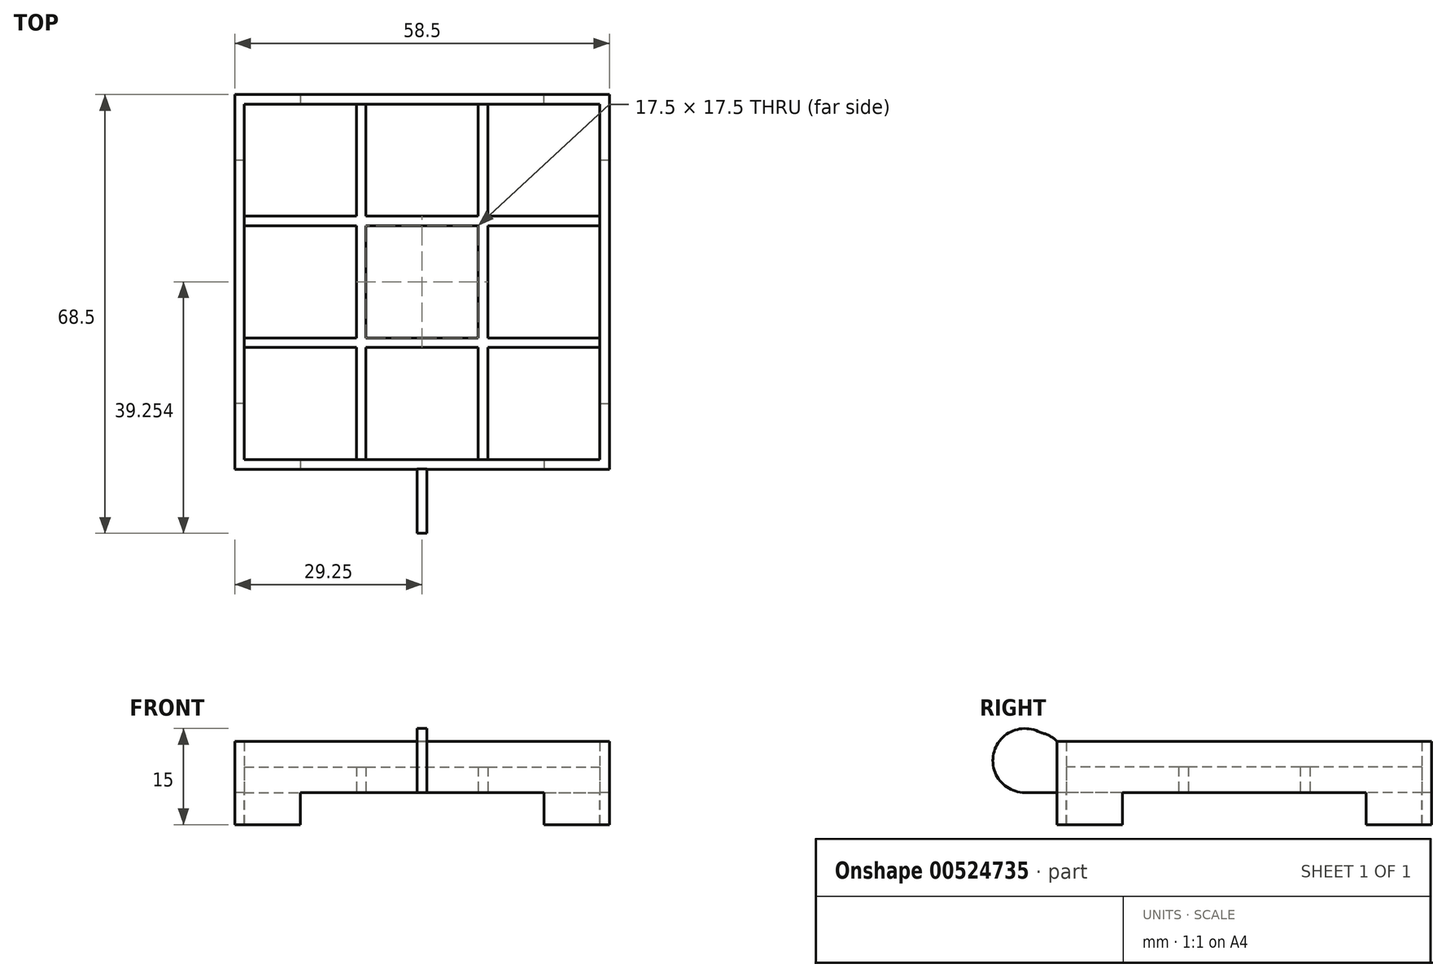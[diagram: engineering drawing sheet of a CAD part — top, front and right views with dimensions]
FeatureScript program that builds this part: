
annotation { "Feature Type Name" : "Feature", "Feature Type Description" : "" }
export const myFeature = defineFeature(function(context is Context, id is Id, definition is map)
    precondition{}
    {
        {
            var Q0;
            Q0=qCreatedBy(makeId("Top.planeOp"),FACE);
            var sketch = newSketch(context, id + "F0", { "sketchPlane" : qUnion([Q0])});
            skLineSegment(sketch, "E0.bottom", {"start": v(-41.53, 34.87) * mm, "end": v(-24.03, 34.87) * mm});
            skLineSegment(sketch, "E0.top", {"start": v(-41.53, 17.37) * mm, "end": v(-24.03, 17.37) * mm});
            skLineSegment(sketch, "E0.left", {"start": v(-41.53, 34.87) * mm, "end": v(-41.53, 17.37) * mm});
            skLineSegment(sketch, "E0.right", {"start": v(-24.03, 34.87) * mm, "end": v(-24.03, 17.37) * mm});
            skLineSegment(sketch, "E1.0.1.0", {"start": v(-41.53, 15.87) * mm, "end": v(-41.53, -1.63) * mm});
            skLineSegment(sketch, "E1.0.1.1", {"start": v(-41.53, -1.63) * mm, "end": v(-24.03, -1.63) * mm});
            skLineSegment(sketch, "E1.0.1.2", {"start": v(-24.03, 15.87) * mm, "end": v(-24.03, -1.63) * mm});
            skLineSegment(sketch, "E1.0.1.3", {"start": v(-41.53, 15.87) * mm, "end": v(-24.03, 15.87) * mm});
            skLineSegment(sketch, "E1.0.2.0", {"start": v(-41.53, -3.13) * mm, "end": v(-41.53, -20.63) * mm});
            skLineSegment(sketch, "E1.0.2.1", {"start": v(-41.53, -20.63) * mm, "end": v(-24.03, -20.63) * mm});
            skLineSegment(sketch, "E1.0.2.2", {"start": v(-24.03, -3.13) * mm, "end": v(-24.03, -20.63) * mm});
            skLineSegment(sketch, "E1.0.2.3", {"start": v(-41.53, -3.13) * mm, "end": v(-24.03, -3.13) * mm});
            skLineSegment(sketch, "E1.1.0.0", {"start": v(-22.53, 34.87) * mm, "end": v(-22.53, 17.37) * mm});
            skLineSegment(sketch, "E1.1.0.1", {"start": v(-22.53, 17.37) * mm, "end": v(-5.03, 17.37) * mm});
            skLineSegment(sketch, "E1.1.0.2", {"start": v(-5.03, 34.87) * mm, "end": v(-5.03, 17.37) * mm});
            skLineSegment(sketch, "E1.1.0.3", {"start": v(-22.53, 34.87) * mm, "end": v(-5.03, 34.87) * mm});
            skLineSegment(sketch, "E1.1.1.0", {"start": v(-22.53, 15.87) * mm, "end": v(-22.53, -1.63) * mm});
            skLineSegment(sketch, "E1.1.1.1", {"start": v(-22.53, -1.63) * mm, "end": v(-5.03, -1.63) * mm});
            skLineSegment(sketch, "E1.1.1.2", {"start": v(-5.03, 15.87) * mm, "end": v(-5.03, -1.63) * mm});
            skLineSegment(sketch, "E1.1.1.3", {"start": v(-22.53, 15.87) * mm, "end": v(-5.03, 15.87) * mm});
            skLineSegment(sketch, "E1.1.2.0", {"start": v(-22.53, -3.13) * mm, "end": v(-22.53, -20.63) * mm});
            skLineSegment(sketch, "E1.1.2.1", {"start": v(-22.53, -20.63) * mm, "end": v(-5.03, -20.63) * mm});
            skLineSegment(sketch, "E1.1.2.2", {"start": v(-5.03, -3.13) * mm, "end": v(-5.03, -20.63) * mm});
            skLineSegment(sketch, "E1.1.2.3", {"start": v(-22.53, -3.13) * mm, "end": v(-5.03, -3.13) * mm});
            skLineSegment(sketch, "E1.2.0.0", {"start": v(-3.53, 34.87) * mm, "end": v(-3.53, 17.37) * mm});
            skLineSegment(sketch, "E1.2.0.1", {"start": v(-3.53, 17.37) * mm, "end": v(13.97, 17.37) * mm});
            skLineSegment(sketch, "E1.2.0.2", {"start": v(13.97, 34.87) * mm, "end": v(13.97, 17.37) * mm});
            skLineSegment(sketch, "E1.2.0.3", {"start": v(-3.53, 34.87) * mm, "end": v(13.97, 34.87) * mm});
            skLineSegment(sketch, "E1.2.1.0", {"start": v(-3.53, 15.87) * mm, "end": v(-3.53, -1.63) * mm});
            skLineSegment(sketch, "E1.2.1.1", {"start": v(-3.53, -1.63) * mm, "end": v(13.97, -1.63) * mm});
            skLineSegment(sketch, "E1.2.1.2", {"start": v(13.97, 15.87) * mm, "end": v(13.97, -1.63) * mm});
            skLineSegment(sketch, "E1.2.1.3", {"start": v(-3.53, 15.87) * mm, "end": v(13.97, 15.87) * mm});
            skLineSegment(sketch, "E1.2.2.0", {"start": v(-3.53, -3.13) * mm, "end": v(-3.53, -20.63) * mm});
            skLineSegment(sketch, "E1.2.2.1", {"start": v(-3.53, -20.63) * mm, "end": v(13.97, -20.63) * mm});
            skLineSegment(sketch, "E1.2.2.2", {"start": v(13.97, -3.13) * mm, "end": v(13.97, -20.63) * mm});
            skLineSegment(sketch, "E1.2.2.3", {"start": v(-3.53, -3.13) * mm, "end": v(13.97, -3.13) * mm});
            skLineSegment(sketch, "E1.direction1", {"start": v(-41.53, 17.37) * mm, "end": v(-22.53, 17.37) * mm, "construction": true});
            skLineSegment(sketch, "E1.direction2", {"start": v(-41.53, 17.37) * mm, "end": v(-41.53, -1.63) * mm, "construction": true});
            skLineSegment(sketch, "E2.bottom", {"start": v(-43.03, 36.37) * mm, "end": v(15.47, 36.37) * mm});
            skLineSegment(sketch, "E2.top", {"start": v(-43.03, -22.13) * mm, "end": v(15.47, -22.13) * mm});
            skLineSegment(sketch, "E2.left", {"start": v(-43.03, 36.37) * mm, "end": v(-43.03, -22.13) * mm});
            skLineSegment(sketch, "E2.right", {"start": v(15.47, 36.37) * mm, "end": v(15.47, -22.13) * mm});
            skSolve(sketch);
        }
        {
            var Q0;
            Q0=makeQuery(id+"F0.imprint","IMPRINT",FACE,{"disambiguationData":[TD([[makeQuery(id+"F0.imprint","IMPRINT",EDGE,{"derivedFrom":sQuery(id+"F0.wireOp",EDGE,"E0.bottom")}),1.0]])]});
            extrude(context, id + "F1", {"entities" : qUnion([Q0]), "depth" : 4 * mm, "offsetDistance" : 25 * mm});
        }
        {
            var Q0;
            Q0=makeQuery(id+"F1.opExtrude","SWEPT_FACE",FACE,{"disambiguationData":[OSD([sQuery(id+"F0.wireOp",EDGE,"E2.top")])]});
            var sketch = newSketch(context, id + "F2", { "sketchPlane" : qUnion([Q0])});
            skLineSegment(sketch, "E3.bottom", {"start": v(-14.53, 0) * mm, "end": v(-13.03, 0) * mm});
            skLineSegment(sketch, "E3.top", {"start": v(-14.53, 10) * mm, "end": v(-13.03, 10) * mm});
            skLineSegment(sketch, "E3.left", {"start": v(-14.53, 0) * mm, "end": v(-14.53, 10) * mm});
            skLineSegment(sketch, "E3.right", {"start": v(-13.03, 0) * mm, "end": v(-13.03, 10) * mm});
            skSolve(sketch);
        }
        {
            var Q0;
            Q0 = qSketchRegion(id + "F2", true);
            extrude(context, id + "F3", {"entities" : qUnion([Q0]), "operationType" : NewBodyOperationType.ADD, "depth" : 10 * mm, "offsetDistance" : 25 * mm});
        }
        {
            var Q0;
            Q0=makeQuery(id+"F3.opExtrude","CAP_EDGE",EDGE,{"disambiguationData":[OSD([sQuery(id+"F2.wireOp",EDGE,"E3.top")])],"isStart":false});
            var Q1;
            Q1=makeQuery(id+"F3.opExtrude","CAP_EDGE",EDGE,{"disambiguationData":[OSD([sQuery(id+"F2.wireOp",EDGE,"E3.bottom")])],"isStart":false});
            var Q2;
            Q2=makeQuery(id+"F3.opExtrude","CAP_EDGE",EDGE,{"disambiguationData":[OSD([sQuery(id+"F2.wireOp",EDGE,"E3.top")])],"isStart":true});
            fillet(context, id + "F4", {"entities" : qUnion([Q0, Q1, Q2]), "radius" : 5 * mm, "tangentPropagation" : true, "allowEdgeOverflow" : false});
        }
        {
            var Q0;
            Q0=makeQuery(id+"F3.opExtrude","SWEPT_FACE",FACE,{"disambiguationData":[OSD([sQuery(id+"F2.wireOp",EDGE,"E3.left")])]});
            var sketch = newSketch(context, id + "F5", { "sketchPlane" : qUnion([Q0])});
            skLineSegment(sketch, "E4.bottom", {"start": v(22.13, 4) * mm, "end": v(20.63, 4) * mm});
            skLineSegment(sketch, "E4.top", {"start": v(22.13, 9.36) * mm, "end": v(20.63, 9.36) * mm});
            skLineSegment(sketch, "E4.left", {"start": v(22.13, 4) * mm, "end": v(22.13, 5) * mm});
            skLineSegment(sketch, "E4.right", {"start": v(20.63, 4) * mm, "end": v(20.63, 9.36) * mm});
            skArc(sketch, "E5", {"start": v(24.67, 9.36) * mm, "mid": v(22.8, 7.52) * mm, "end": v(22.13, 5) * mm});
            skLineSegment(sketch, "E6", {"start": v(22.13, 9.36) * mm, "end": v(24.67, 9.36) * mm});
            skSolve(sketch);
        }
        {
            var Q0;
            Q0 = qSketchRegion(id + "F5", true);
            extrude(context, id + "F6", {"entities" : qUnion([Q0]), "operationType" : NewBodyOperationType.ADD, "oppositeDirection" : true, "depth" : 1.5 * mm, "offsetDistance" : 25 * mm});
        }
        {
            var Q0;
            Q0=makeQuery(id+"F6.opExtrude","SWEPT_EDGE",EDGE,{"disambiguationData":[OSD([sQuery(id+"F5.wireOp",EDGE,"E4.top"),sQuery(id+"F5.wireOp",EDGE,"E4.right")])]});
            fillet(context, id + "F7", {"entities" : qUnion([Q0]), "radius" : 5 * mm, "tangentPropagation" : true, "allowEdgeOverflow" : false});
        }
        {
            var Q0;
            Q0=makeQuery(id+"F7.opFillet","BLEND_EDGE",EDGE,{"blendedFrom":[makeQuery(id+"F6.opExtrude","SWEPT_EDGE",EDGE,{"disambiguationData":[OSD([sQuery(id+"F5.wireOp",EDGE,"E4.top"),sQuery(id+"F5.wireOp",EDGE,"E4.right")])]}),makeQuery(id+"F4.opFillet","BLEND_FACE",FACE,{"disambiguationData":[OSD([sQuery(id+"F2.wireOp",EDGE,"E3.bottom")])]})],"blendedInto":[makeQuery(id+"F4.opFillet","BLEND_FACE",FACE,{"disambiguationData":[OSD([sQuery(id+"F2.wireOp",EDGE,"E3.bottom")])]})]});
            fillet(context, id + "F8", {"entities" : qUnion([Q0]), "radius" : 5 * mm, "tangentPropagation" : true, "allowEdgeOverflow" : false});
        }
        {
            var Q0;
            Q0=makeQuery(id+"F1.opExtrude","CAP_FACE",FACE,{"disambiguationData":[OSD([sQuery(id+"F0.wireOp",EDGE,"E0.bottom"),sQuery(id+"F0.wireOp",EDGE,"E0.top"),sQuery(id+"F0.wireOp",EDGE,"E0.left"),sQuery(id+"F0.wireOp",EDGE,"E0.right"),sQuery(id+"F0.wireOp",EDGE,"E1.0.1.0"),sQuery(id+"F0.wireOp",EDGE,"E1.0.1.1"),sQuery(id+"F0.wireOp",EDGE,"E1.0.1.2"),sQuery(id+"F0.wireOp",EDGE,"E1.0.1.3"),sQuery(id+"F0.wireOp",EDGE,"E1.0.2.0"),sQuery(id+"F0.wireOp",EDGE,"E1.0.2.1"),sQuery(id+"F0.wireOp",EDGE,"E1.0.2.2"),sQuery(id+"F0.wireOp",EDGE,"E1.0.2.3"),sQuery(id+"F0.wireOp",EDGE,"E1.1.0.0"),sQuery(id+"F0.wireOp",EDGE,"E1.1.0.1"),sQuery(id+"F0.wireOp",EDGE,"E1.1.0.2"),sQuery(id+"F0.wireOp",EDGE,"E1.1.0.3"),sQuery(id+"F0.wireOp",EDGE,"E1.1.1.0"),sQuery(id+"F0.wireOp",EDGE,"E1.1.1.1"),sQuery(id+"F0.wireOp",EDGE,"E1.1.1.2"),sQuery(id+"F0.wireOp",EDGE,"E1.1.1.3"),sQuery(id+"F0.wireOp",EDGE,"E1.1.2.0"),sQuery(id+"F0.wireOp",EDGE,"E1.1.2.1"),sQuery(id+"F0.wireOp",EDGE,"E1.1.2.2"),sQuery(id+"F0.wireOp",EDGE,"E1.1.2.3"),sQuery(id+"F0.wireOp",EDGE,"E1.2.0.0"),sQuery(id+"F0.wireOp",EDGE,"E1.2.0.1"),sQuery(id+"F0.wireOp",EDGE,"E1.2.0.2"),sQuery(id+"F0.wireOp",EDGE,"E1.2.0.3"),sQuery(id+"F0.wireOp",EDGE,"E1.2.1.0"),sQuery(id+"F0.wireOp",EDGE,"E1.2.1.1"),sQuery(id+"F0.wireOp",EDGE,"E1.2.1.2"),sQuery(id+"F0.wireOp",EDGE,"E1.2.1.3"),sQuery(id+"F0.wireOp",EDGE,"E1.2.2.0"),sQuery(id+"F0.wireOp",EDGE,"E1.2.2.1"),sQuery(id+"F0.wireOp",EDGE,"E1.2.2.2"),sQuery(id+"F0.wireOp",EDGE,"E1.2.2.3"),sQuery(id+"F0.wireOp",EDGE,"E2.bottom"),sQuery(id+"F0.wireOp",EDGE,"E2.top"),sQuery(id+"F0.wireOp",EDGE,"E2.left"),sQuery(id+"F0.wireOp",EDGE,"E2.right")])],"isStart":false});
            var sketch = newSketch(context, id + "F9", { "sketchPlane" : qUnion([Q0])});
            skLineSegment(sketch, "E7.bottom", {"start": v(-43.03, 36.37) * mm, "end": v(15.47, 36.37) * mm});
            skLineSegment(sketch, "E7.top", {"start": v(-43.03, -22.13) * mm, "end": v(15.47, -22.13) * mm});
            skLineSegment(sketch, "E7.left", {"start": v(-43.03, 36.37) * mm, "end": v(-43.03, -22.13) * mm});
            skLineSegment(sketch, "E7.right", {"start": v(15.47, 36.37) * mm, "end": v(15.47, -22.13) * mm});
            skLineSegment(sketch, "E8.bottom", {"start": v(-41.53, 34.87) * mm, "end": v(13.97, 34.87) * mm});
            skLineSegment(sketch, "E8.top", {"start": v(-41.53, -20.63) * mm, "end": v(13.97, -20.63) * mm});
            skLineSegment(sketch, "E8.left", {"start": v(-41.53, 34.87) * mm, "end": v(-41.53, -20.63) * mm});
            skLineSegment(sketch, "E8.right", {"start": v(13.97, 34.87) * mm, "end": v(13.97, -20.63) * mm});
            skSolve(sketch);
        }
        {
            var Q0;
            Q0 = qSketchRegion(id + "F9", true);
            extrude(context, id + "F10", {"entities" : qUnion([Q0]), "operationType" : NewBodyOperationType.ADD, "depth" : 4 * mm, "offsetDistance" : 25 * mm});
        }
        {
            var Q0;
            Q0=makeQuery(id+"F3.boolean.opBoolean","MERGE",FACE,{"derivedFrom":[makeQuery(id+"F1.opExtrude","CAP_FACE",FACE,{"disambiguationData":[OSD([sQuery(id+"F0.wireOp",EDGE,"E0.bottom"),sQuery(id+"F0.wireOp",EDGE,"E0.top"),sQuery(id+"F0.wireOp",EDGE,"E0.left"),sQuery(id+"F0.wireOp",EDGE,"E0.right"),sQuery(id+"F0.wireOp",EDGE,"E1.0.1.0"),sQuery(id+"F0.wireOp",EDGE,"E1.0.1.1"),sQuery(id+"F0.wireOp",EDGE,"E1.0.1.2"),sQuery(id+"F0.wireOp",EDGE,"E1.0.1.3"),sQuery(id+"F0.wireOp",EDGE,"E1.0.2.0"),sQuery(id+"F0.wireOp",EDGE,"E1.0.2.1"),sQuery(id+"F0.wireOp",EDGE,"E1.0.2.2"),sQuery(id+"F0.wireOp",EDGE,"E1.0.2.3"),sQuery(id+"F0.wireOp",EDGE,"E1.1.0.0"),sQuery(id+"F0.wireOp",EDGE,"E1.1.0.1"),sQuery(id+"F0.wireOp",EDGE,"E1.1.0.2"),sQuery(id+"F0.wireOp",EDGE,"E1.1.0.3"),sQuery(id+"F0.wireOp",EDGE,"E1.1.1.0"),sQuery(id+"F0.wireOp",EDGE,"E1.1.1.1"),sQuery(id+"F0.wireOp",EDGE,"E1.1.1.2"),sQuery(id+"F0.wireOp",EDGE,"E1.1.1.3"),sQuery(id+"F0.wireOp",EDGE,"E1.1.2.0"),sQuery(id+"F0.wireOp",EDGE,"E1.1.2.1"),sQuery(id+"F0.wireOp",EDGE,"E1.1.2.2"),sQuery(id+"F0.wireOp",EDGE,"E1.1.2.3"),sQuery(id+"F0.wireOp",EDGE,"E1.2.0.0"),sQuery(id+"F0.wireOp",EDGE,"E1.2.0.1"),sQuery(id+"F0.wireOp",EDGE,"E1.2.0.2"),sQuery(id+"F0.wireOp",EDGE,"E1.2.0.3"),sQuery(id+"F0.wireOp",EDGE,"E1.2.1.0"),sQuery(id+"F0.wireOp",EDGE,"E1.2.1.1"),sQuery(id+"F0.wireOp",EDGE,"E1.2.1.2"),sQuery(id+"F0.wireOp",EDGE,"E1.2.1.3"),sQuery(id+"F0.wireOp",EDGE,"E1.2.2.0"),sQuery(id+"F0.wireOp",EDGE,"E1.2.2.1"),sQuery(id+"F0.wireOp",EDGE,"E1.2.2.2"),sQuery(id+"F0.wireOp",EDGE,"E1.2.2.3"),sQuery(id+"F0.wireOp",EDGE,"E2.bottom"),sQuery(id+"F0.wireOp",EDGE,"E2.top"),sQuery(id+"F0.wireOp",EDGE,"E2.left"),sQuery(id+"F0.wireOp",EDGE,"E2.right")])],"isStart":true}),makeQuery(id+"F3.opExtrude","SWEPT_FACE",FACE,{"disambiguationData":[OSD([sQuery(id+"F2.wireOp",EDGE,"E3.bottom")])]})]});
            var sketch = newSketch(context, id + "F11", { "sketchPlane" : qUnion([Q0])});
            skLineSegment(sketch, "E9.bottom", {"start": v(-41.53, 11.88) * mm, "end": v(-43.03, 11.88) * mm});
            skLineSegment(sketch, "E9.top", {"start": v(-41.53, 22.13) * mm, "end": v(-43.03, 22.13) * mm});
            skLineSegment(sketch, "E9.left", {"start": v(-41.53, 11.88) * mm, "end": v(-41.53, 20.63) * mm});
            skLineSegment(sketch, "E9.right", {"start": v(-43.03, 11.88) * mm, "end": v(-43.03, 22.13) * mm});
            skLineSegment(sketch, "E10.bottom", {"start": v(-32.78, 20.63) * mm, "end": v(-41.53, 20.63) * mm});
            skLineSegment(sketch, "E10.top", {"start": v(-32.78, 22.13) * mm, "end": v(-41.53, 22.13) * mm});
            skLineSegment(sketch, "E10.left", {"start": v(-32.78, 20.63) * mm, "end": v(-32.78, 22.13) * mm});
            skLineSegment(sketch, "E11.bottom", {"start": v(5.22, 20.63) * mm, "end": v(13.97, 20.63) * mm});
            skLineSegment(sketch, "E11.top", {"start": v(5.22, 22.13) * mm, "end": v(13.97, 22.13) * mm});
            skLineSegment(sketch, "E11.left", {"start": v(5.22, 20.63) * mm, "end": v(5.22, 22.13) * mm});
            skLineSegment(sketch, "E12.bottom", {"start": v(13.97, 11.88) * mm, "end": v(15.47, 11.88) * mm});
            skLineSegment(sketch, "E12.top", {"start": v(13.97, 22.13) * mm, "end": v(15.47, 22.13) * mm});
            skLineSegment(sketch, "E12.left", {"start": v(13.97, 11.88) * mm, "end": v(13.97, 20.63) * mm});
            skLineSegment(sketch, "E12.right", {"start": v(15.47, 11.88) * mm, "end": v(15.47, 22.13) * mm});
            skLineSegment(sketch, "E13.bottom", {"start": v(-32.78, -36.37) * mm, "end": v(-43.03, -36.37) * mm});
            skLineSegment(sketch, "E13.top", {"start": v(-32.78, -34.87) * mm, "end": v(-41.53, -34.87) * mm});
            skLineSegment(sketch, "E13.left", {"start": v(-32.78, -36.37) * mm, "end": v(-32.78, -34.87) * mm});
            skLineSegment(sketch, "E13.right", {"start": v(-43.03, -36.37) * mm, "end": v(-43.03, -34.87) * mm});
            skPoint(sketch, "E14.oppositeSnap0", {"position": v(-41.53, -26.12) * mm});
            skLineSegment(sketch, "E14.top", {"start": v(-41.53, -26.12) * mm, "end": v(-43.03, -26.12) * mm});
            skLineSegment(sketch, "E14.left", {"start": v(-41.53, -34.87) * mm, "end": v(-41.53, -26.12) * mm});
            skLineSegment(sketch, "E14.right", {"start": v(-43.03, -34.87) * mm, "end": v(-43.03, -26.12) * mm});
            skLineSegment(sketch, "E15.bottom", {"start": v(5.22, -34.87) * mm, "end": v(13.97, -34.87) * mm});
            skLineSegment(sketch, "E15.top", {"start": v(5.22, -36.37) * mm, "end": v(15.47, -36.37) * mm});
            skLineSegment(sketch, "E15.left", {"start": v(5.22, -34.87) * mm, "end": v(5.22, -36.37) * mm});
            skLineSegment(sketch, "E15.right", {"start": v(15.47, -34.87) * mm, "end": v(15.47, -36.37) * mm});
            skLineSegment(sketch, "E16.top", {"start": v(15.47, -26.12) * mm, "end": v(13.97, -26.12) * mm});
            skLineSegment(sketch, "E16.left", {"start": v(15.47, -34.87) * mm, "end": v(15.47, -26.12) * mm});
            skLineSegment(sketch, "E16.right", {"start": v(13.97, -34.87) * mm, "end": v(13.97, -26.12) * mm});
            skSolve(sketch);
        }
        {
            var Q0;
            Q0 = qSketchRegion(id + "F11", true);
            extrude(context, id + "F12", {"entities" : qUnion([Q0]), "operationType" : NewBodyOperationType.ADD, "depth" : 5 * mm, "offsetDistance" : 25 * mm});
        }
    });
